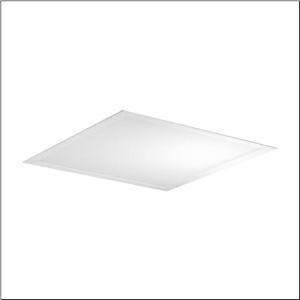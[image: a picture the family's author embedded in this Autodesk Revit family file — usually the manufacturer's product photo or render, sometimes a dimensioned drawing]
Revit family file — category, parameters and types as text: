
# Revit family: apollon_r__21_square_51mq11wc2454_d0b3
name_source: partatom
category: Lighting Fixtures
units: mm (PartAtom-declared; Revit-internal decimal feet)

## family parameters
Cut with Voids When Loaded = No
Host = Face
Light Source = No
Part Type = Normal
Room Calculation Point = No
Round Connector Dimension = Use Diameter
Shared = No

## types (1)
- Apollon® 21 square (1 x LED, 4200 lm, 24.7 W, 4000K)
    Apparent Load = 25 VA
    CIE Flux Codes = 60 87 97 100 100
    Color Rendering = 80
    Color Temperature = 4000K
    Default Elevation = 1800 mm
    Description = Apollon® 21 square, office luminaire, primary optical cover: micro prismatic cover, of PMMA, CAT 2 (L<= 3000cd/m²), light emission: direct distribution, primary light characteristic: symmetric, installation type: lay-in mounting, LED, rated luminous flux: 4.200lm, luminous efficacy: 170lm/W, light colour: 840, colour temperature: 4000K, with terminal, 5-pole, mains connection: 220..240V, AC/DC, 0/50..60Hz, rated input power: 24.7W, housing, of aluminium, coated, traffic white (RAL 9016), module: M625, length: 620mm, width: 620mm, height: 30mm, housing upper side, of sheet steel, galvanised, protection rating (complete): IP20, protection rating (lamp compartment, on room side): IP54, insulation class (complete): insulation class II (safety insulation), certification: CE, ENEC, impact resistance: IK03, permissible operating ambient temperature: -20..+45°C, permissible storage temperature: -40..+80°C, packaging unit: 1 piece
    Height = 0 mm  [stored 0 ft]
    Lamp = 1 x LED
    Lamp Light Flux = 4200 lm
    Lamp Power = 24.7 W
    Lamp count = 1
    Length = 620 mm
    Luminous efficacy = 170 lm/W
    Manufacturer = Siteco
    ModVariant = No
    Model = 51MQ11WC2454
    Mounting Place = Ceiling
    Mounting Type = Recessed
    Number of Poles = 1
    OnlyDefault = Yes
    Power Factor = 1
    Product Name = Apollon® 21 square
    Product group = office luminaire | ceiling recessed
    ProductGroupID = 401
    Protection Class = Protection class II
    Protection Degree = IP 20
    RLX_Detail_Level = 1
    RLX_Emergency_Light_Flux = 0 lm
    RLX_Emergency_Type = 0
    RLX_Emergency_Type_DB = No
    RlxData = <blob elided: 12957 chars, md5=2514bdb9>
    Socket = socket
    Standby Power = 0 W
    System Light Flux = 4200 lm
    System Power = 25 W
    Type Comments = Product without accessories
    Type Image = l_1291054.jpg
    URL = http://relux.com
    VarID = ---
    Voltage = 0 V
    Weight = 0.00 kg
    Width = 620 mm

note: [stored X ft] marks values corroborated as IEEE doubles in the binary element streams (Revit-internal decimal feet)

## geometry (parser evidence)
native form markers: Sweep x11
no freeform markers — native parametric forms only
